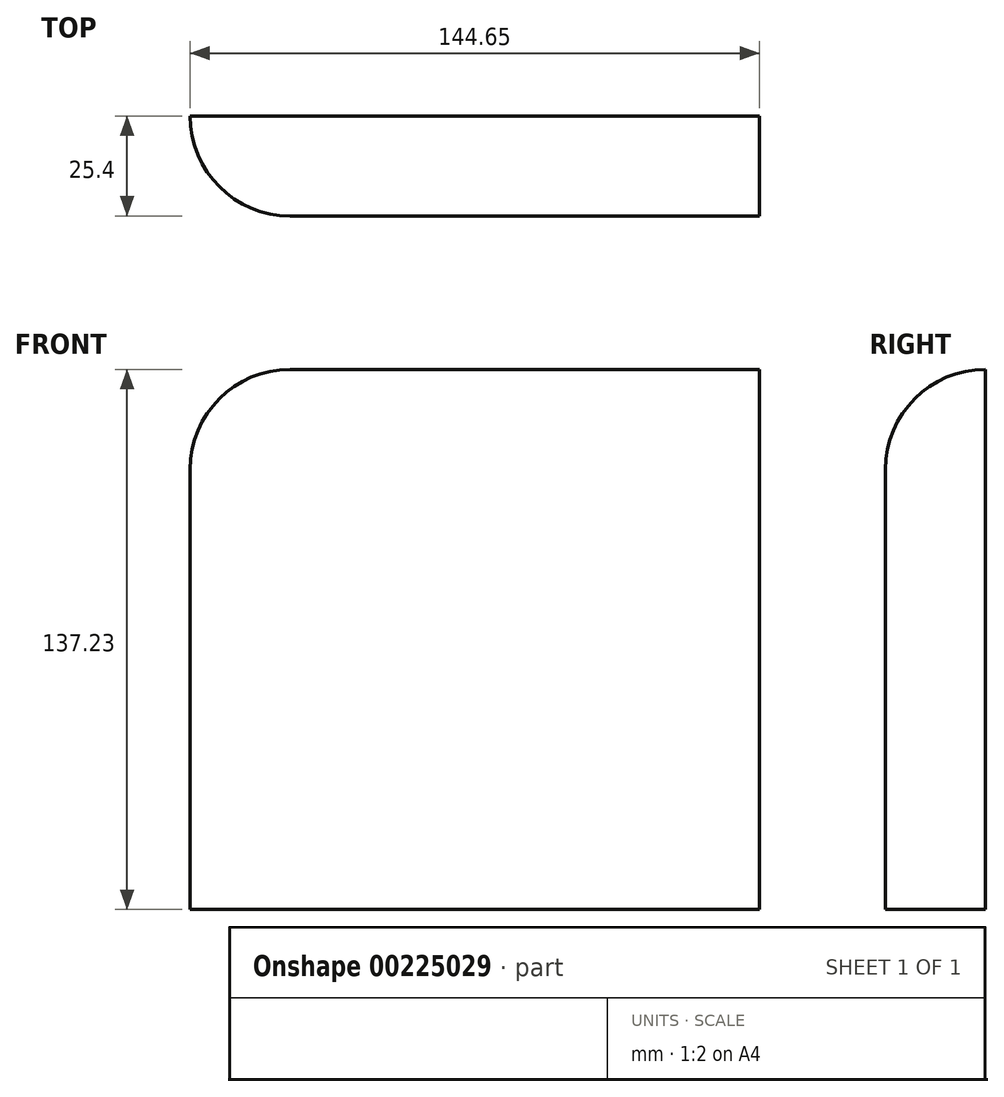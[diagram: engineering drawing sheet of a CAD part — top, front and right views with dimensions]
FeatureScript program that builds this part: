
annotation { "Feature Type Name" : "Feature", "Feature Type Description" : "" }
export const myFeature = defineFeature(function(context is Context, id is Id, definition is map)
    precondition{}
    {
        {
            var Q0;
            Q0=qCreatedBy(makeId("Front.planeOp"),FACE);
            var sketch = newSketch(context, id + "F0", { "sketchPlane" : qUnion([Q0])});
            skLineSegment(sketch, "E0.bottom", {"start": v(-48.98, 55.87) * mm, "end": v(95.67, 55.87) * mm});
            skLineSegment(sketch, "E0.top", {"start": v(-48.98, -81.36) * mm, "end": v(95.67, -81.36) * mm});
            skLineSegment(sketch, "E0.left", {"start": v(-48.98, 55.87) * mm, "end": v(-48.98, -81.36) * mm});
            skLineSegment(sketch, "E0.right", {"start": v(95.67, 55.87) * mm, "end": v(95.67, -81.36) * mm});
            skSolve(sketch);
        }
        {
            var Q0;
            Q0 = qSketchRegion(id + "F0", true);
            extrude(context, id + "F2", {"entities" : qUnion([Q0]), "depth" : 25.4 * mm});
        }
        {
            var Q0;
            Q0=makeQuery(id+"F2.opExtrude","SWEPT_EDGE",EDGE,{"disambiguationData":[OSD([sQuery(id+"F0.wireOp",EDGE,"E0.bottom"),sQuery(id+"F0.wireOp",EDGE,"E0.left")])]});
            var Q1;
            Q1=makeQuery(id+"F2.opExtrude","CAP_EDGE",EDGE,{"disambiguationData":[OSD([sQuery(id+"F0.wireOp",EDGE,"E0.bottom")])],"isStart":false});
            var Q2;
            Q2=makeQuery(id+"F2.opExtrude","CAP_EDGE",EDGE,{"disambiguationData":[OSD([sQuery(id+"F0.wireOp",EDGE,"E0.left")])],"isStart":false});
            fillet(context, id + "F1", {"entities" : qUnion([Q0, Q1, Q2]), "radius" : 25.4 * mm, "tangentPropagation" : true, "allowEdgeOverflow" : false});
        }
    });
